# Revit family: Innovo  BENL_IR 20 160 BENL NAT
name_source: partatom
category: Mechanical Equipment
revit_build: Autodesk Revit 2015 (Build: 20160512_0715(x64)
units: mm (PartAtom-declared; Revit-internal decimal feet)

## types (1)
- IR-20-160 BENL NAT
    1e Onderhoud (check-up) = 3 maanden na installatie
    2e Onderhoud (algeheel onderhoud) = 12 maanden na installatie
    Aansluiting Aftapkraan = 3/4"
    Aansluiting Condensafvoer = 40 mm  [stored 0.131234 ft]
    Aansluiting Koud Water = 3/4"
    Aansluiting T&P = 3/4"
    Aansluiting Warm Water = 3/4"
    Ander capaciteitsprofiel = -
    Assembly Code = D3010
    BIM Content Developer = CAD & Company
    Bestemming / Land = BelgIë
    Breedte = 560 mm  [stored 1.83727 ft]
    CE-PIN = 0063CQ3037
    CO2-uitstoot (tol. +/- 1.0) vol% = 9.3/7.5
    Capaciteitsprofiel = XL
    Description = Condenserende Hoog Rendementsboiler
    Diameter = 560 mm  [stored 1.83727 ft]
    Diameter Schoorsteen - boiler = 80/125 mm/mm
    Diameter Schoorsteen - concentrisch systeem = 80/125 mm/mm
    Diameter Schoorsteen - parallel systeem = 2x80
    Elektrisch Vermogen (nominaal) = 36 W
    Elektrisch Vermogen (piek) = 85 W
    Energie-efficiëntie voor waterverwarming (1) = 92%
    Energie-efficiëntie voor waterverwarming (2) = -
    Energie-efficiëntieklasse voor waterverwarming (1) = A
    Energie-efficiëntieklasse voor waterverwarming (2) = -
    Fabrikantnummer = E 7110
    Fase = 1
    Frequentie = 50 Hz
    Garrantie op Onderdelen = 12 maanden
    Garrantie op Tank = 36 maanden
    Gas Aansluiting = 15"
    Gas Voordruk = 2000/2500 Pa
    Gascategorie = I2E(S)B
    Gasverbruik - Massa kg/h = n.v.t.
    Gasverbruik - Volume ltr/hr = 1.90/1.80
    Geluidsniveau binnen = 52 dB
    Geluidsniveau dB (A) = <45
    Handelsmerk = A.O. Smith
    Hoogte = 1270 mm
    Hoogte Gas Aansluiting = 860 mm
    Hoogte Koud Water Inlaat = 170 mm  [stored 0.557743 ft]
    Hoogte Lucht Inlaat = 1295 mm
    Hoogte Rookgasafvoer = 1295 mm
    Hoogte Warm Water Uitlaat = 1270 mm
    Inhoud = 160.0 L
    Installatie Typen = B23/C13/C33/C43/C53/C63
    Isolatiedikte = 50 mm  [stored 0.164042 ft]
    Jaarlijks brandstofverbruik (1) = 16 GJ GCV
    Jaarlijks brandstofverbruik (2) = -
    Jaarlijks elektriciteitsverbruik (1) = 37 kWh
    Jaarlijks elektriciteitsverbruik (2) = -
    Kraan Hoogte 01 = 604 mm  [stored 1.98163 ft]
    Kraan Hoogte 02 = 1070 mm  [stored 3.5105 ft]
    Ledig Gewicht = 95 kg
    Length = 780 mm  [stored 2.55906 ft]
    Manufacturer = A.O. Smith Water Products Company b.v.
    Max. Rookgastemperatuur = 61 °C
    Max. Stand Regelthermostaat = 85 °C
    Max. Werkdruk = 800000.0 Pa
    Min. Stand Regelthermostaat = 40 °C
    Model = IR-20-160 BENL NAT
    NOx-uitstoot (lucht vrij, 0% O2) ppm = 19.0/18.0
    NOx-uitstoot mg/kWh = 30.0/29.0
    Nominaal Vermogen = 19100.0/15800.0
    Nominale Belasting (Bovenwaarde) = 20000.0/16600.0
    Nominale Belasting (Onderwaarde) = 18000.0/14900.0
    Onderhoudsinterval = 12 maanden
    Opwarmtijd bij ΔT = 28°C = 11
    Opwarmtijd bij ΔT = 44°C = 17
    Opwarmtijd bij ΔT = 50°C = 19
    Opwarmtijd bij ΔT = 55°C = 21
    Opwarmtijd bij ΔT = 70°C = 27
    Produkt Model Nummer (EAN-nummer) = 8717449286019
    Rendement (Hi, vlgs. NEN-EN 89 - 1999) = 106
    Rendement (Hs, vlgs. NEN-EN 89 - 1999) = 95
    Seizoens Rendement (Hs) = 95
    Setpoint thermostaat = 65 °C
    Slimme controlefunctie = No
    Soort Verpakking = Karton en Hout
    Stand Regelthermostaat = 65 °C
    Standaard Afgesteld op = G20/G25
    Stilstandsverlies = 0 W
    Stilstandsverlies - dagelijks (24u) = 0 W
    Tapcapaciteit Continu bij ΔT = 28°C = 590.0 L/s
    Tapcapaciteit Continu bij ΔT = 44°C = 380.0 L/s
    Tapcapaciteit Continu bij ΔT = 50°C = 330.0 L/s
    Tapcapaciteit Continu bij ΔT = 55°C = 300.0 L/s
    Tapcapaciteit Continu bij ΔT = 70°C = 240.0 L/s
    Tapcapaciteit bij ΔT = 28°C na 120 min. = 1500.0 L
    Tapcapaciteit bij ΔT = 28°C na 30 min. = 530.0 L
    Tapcapaciteit bij ΔT = 28°C na 60 min. = 820.0 L
    Tapcapaciteit bij ΔT = 28°C na 90 min. = 1200.0 L
    Tapcapaciteit bij ΔT = 44°C  na 30 min. = 880.0 L
    Tapcapaciteit bij ΔT = 44°C  na 60 min. = 320.0 L
    Tapcapaciteit bij ΔT = 44°C  na 90 min. = 510.0 L
    Tapcapaciteit bij ΔT = 44°C na 120 min. = 690.0 L
    Tapcapaciteit bij ΔT = 50°C  na 30 min. = 270.0 L
    Tapcapaciteit bij ΔT = 50°C  na 60 min. = 440.0 L
    Tapcapaciteit bij ΔT = 50°C  na 90 min. = 600.0 L
    Tapcapaciteit bij ΔT = 50°C na 120 min. = 770.0 L
    Tapcapaciteit bij ΔT = 55°C  na 120 min. = 700.0 L
    Tapcapaciteit bij ΔT = 55°C  na 30 min. = 240.0 L
    Tapcapaciteit bij ΔT = 55°C  na 60 min. = 390.0 L
    Tapcapaciteit bij ΔT = 55°C  na 90 min. = 540.0 L
    Tapcapaciteit bij ΔT = 70°C  na 120 min. = 520.0 L
    Tapcapaciteit bij ΔT = 70°C  na 30 min. = 170.0 L
    Tapcapaciteit bij ΔT = 70°C  na 60 min. = 290.0 L
    Tapcapaciteit bij ΔT = 70°C  na 90 min. = 410.0 L
    Totaal Gewicht = 274 kg
    Transportgewicht = 114 kg
    Type aanduiding = IR-20-160
    URL = www.aosmith.be
    Uitschakeldruk LDS < = 115
    Uitsluitend werkend in daluren = No
    Verpakkingsbreedte = 786 mm  [stored 2.57874 ft]
    Verpakkingshoogte = 1465 mm
    Verpakkingslengte = 946 mm  [stored 3.10367 ft]
    Voltage = 230 V
    Voorzorgsmaatregelen tijdens montage, installatie of onderhoud = zie Gebruikers, Installatie, Service en Onderhouds handleiding
    Werkruimte Afstand Voor = 1000 mm  [stored 3.28084 ft]
    Werkruimte Hoogte = 2270 mm
    Werkruimte Radius = 730 mm  [stored 2.39501 ft]

note: [stored X ft] marks values corroborated as IEEE doubles in the binary element streams (Revit-internal decimal feet)

## geometry (parser evidence)
native form markers: Blend x26, Sweep x22
no freeform markers — native parametric forms only
